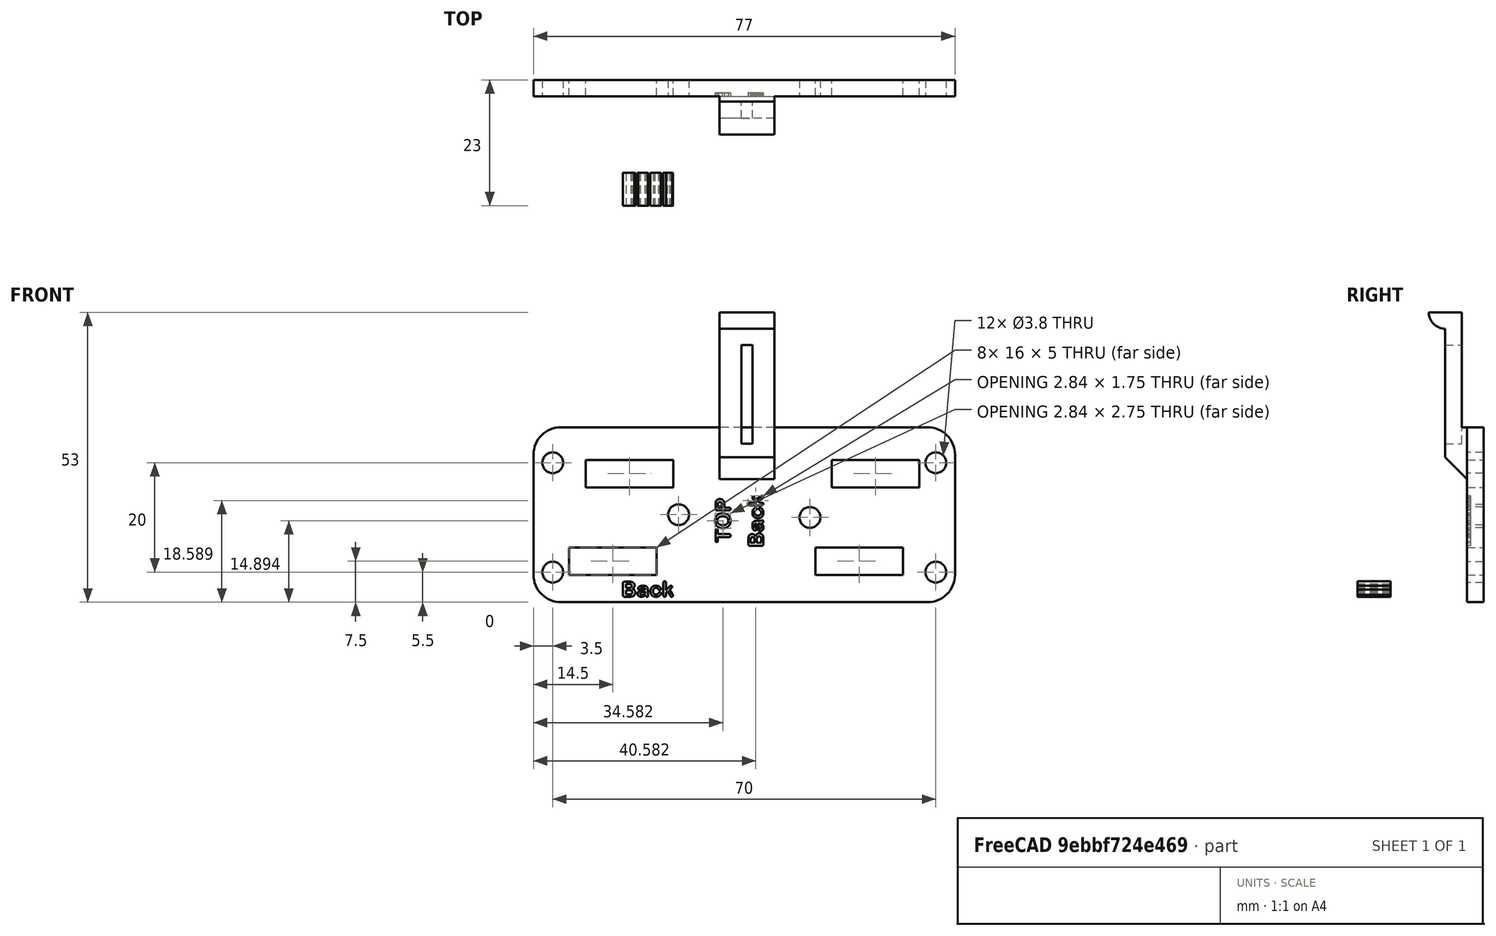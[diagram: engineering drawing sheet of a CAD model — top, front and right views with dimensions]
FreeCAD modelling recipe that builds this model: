
FCSTD DOCUMENT  (FreeCAD 0.16R6712 (Git))
Label: ParkingNozzleBackPlateLeft
License: All rights reserved
LicenseURL: http://en.wikipedia.org/wiki/All_rights_reserved
objects: Part::Cylinder×14, Part::MultiFuse×10, Part::Box×9, Part::Cut×9, Part::Feature×4, Part::Part2DObjectPython×2, Part::Extrusion×1
note: 49 computed .brp shape members not serialized (recipe doc carries the construction recipe); baked Part::Feature solids carry a one-line shape summary decoded from their .brp

FEATURE [Part::Part2DObjectPython] ShapeString002  # Draft 2D object (typed FeaturePython)
  FontFile = <path>
  Size = 3
  String = TOP
  Tracking = 4
FEATURE [Part::Feature] Extrude001002001  label="Extrude001003"
  Placement = pos=(18,0,11) rot=(0,-1,0;1.5708rad)
  shape: bbox 2.835 x 6 x 7.877 mm, 76 faces, 3 solids (baked)
FEATURE [Part::Part2DObjectPython] ShapeString003  # Draft 2D object (typed FeaturePython)
  FontFile = <path>
  Size = 3
  String = Back
  Tracking = 4
FEATURE [Part::Extrusion] Extrude001002002
  Base = -> ShapeString003
  Dir = (0,0,6)
  Placement = pos=(0,0,0) rot=(1,0,0;1.5708rad)
  Solid = false
FEATURE [Part::Feature] Extrude001002002001  label="Extrude001002003"
  Placement = pos=(24,0,10) rot=(0,-1,0;1.5708rad)
  shape: bbox 2.835 x 6 x 9.142 mm, 140 faces, 4 solids (baked)
FEATURE [Part::Box] Box035  label="Würfel034"
  Height = 32
  Length = 77
  Placement = pos=(-16,14,-1) rot=(0,0,1;0rad)
  Width = 3
FEATURE [Part::MultiFuse] Fusion  label="Label"
  Placement = pos=(2,14.6,-1) rot=(0,0,1;0rad)
  Shapes = -> [Extrude001002002001,Extrude001002001]
FEATURE [Part::Cut] Cut
  Base = -> Box035
  Tool = -> Fusion
FEATURE [Part::Box] Box036  label="Würfel035"
  Height = 21
  Length = 10
  Placement = pos=(0,0,-2) rot=(0,0,1;0rad)
  Width = 3
FEATURE [Part::Feature] Cylinder041  label="Zylinder032"
  Placement = pos=(0,0,-2) rot=(1,0,0;1.5708rad)
  shape: bbox 10 x 6 x 3 mm, 4 faces (baked)
FEATURE [Part::MultiFuse] Fusion026007
  Placement = pos=(28,10,50) rot=(0,1,0;3.14159rad)
  Shapes = -> [Box036,Cylinder041]
FEATURE [Part::Cylinder] Cylinder051  label="Zylinder042"
  Angle = 90
  Height = 40
  Placement = pos=(33,25,29) rot=(1,0,0;1.5708rad)
  Radius = 8
FEATURE [Part::Cylinder] Cylinder052  label="Zylinder043"
  Angle = 90
  Height = 40
  Placement = pos=(33,25,29) rot=(1,0,0;1.5708rad)
  Radius = 5
FEATURE [Part::Cut] Cut011004004
  Base = -> Cylinder051
  Placement = pos=(18,0,-7) rot=(0,-1,0;1.5708rad)
  Tool = -> Cylinder052
FEATURE [Part::Cylinder] Cylinder053  label="Zylinder044"
  Angle = 90
  Height = 40
  Placement = pos=(33,25,29) rot=(1,0,0;1.5708rad)
  Radius = 8
FEATURE [Part::Cylinder] Cylinder054  label="Zylinder045"
  Angle = 90
  Height = 40
  Placement = pos=(33,25,29) rot=(1,0,0;1.5708rad)
  Radius = 5
FEATURE [Part::Cut] Cut011004005
  Base = -> Cylinder053
  Placement = pos=(22,0,33) rot=(0,1,0;3.14159rad)
  Tool = -> Cylinder054
FEATURE [Part::Cylinder] Cylinder055  label="Zylinder046"
  Angle = 90
  Height = 40
  Placement = pos=(33,25,29) rot=(1,0,0;1.5708rad)
  Radius = 8
FEATURE [Part::Cylinder] Cylinder056  label="Zylinder047"
  Angle = 90
  Height = 40
  Placement = pos=(33,25,29) rot=(1,0,0;1.5708rad)
  Radius = 5
FEATURE [Part::Cut] Cut011004006
  Base = -> Cylinder055
  Placement = pos=(23,0,-3) rot=(0,0,1;0rad)
  Tool = -> Cylinder056
FEATURE [Part::Cylinder] Cylinder059  label="Zylinder050"
  Angle = 90
  Height = 40
  Placement = pos=(33,25,29) rot=(1,0,0;1.5708rad)
  Radius = 8
FEATURE [Part::Cylinder] Cylinder060  label="Zylinder051"
  Angle = 90
  Height = 40
  Placement = pos=(33,25,29) rot=(1,0,0;1.5708rad)
  Radius = 5
FEATURE [Part::Cut] Cut011004008
  Base = -> Cylinder059
  Placement = pos=(27,0,37) rot=(0,1,0;1.5708rad)
  Tool = -> Cylinder060
FEATURE [Part::MultiFuse] Fusion026012  label="RoundEdges"
  Shapes = -> [Cut011004008,Cut011004006,Cut011004004,Cut011004005]
FEATURE [Part::Box] Box039  label="Würfel038"
  Height = 10
  Length = 10
  Width = 4
FEATURE [Part::Box] Box040  label="Würfel039"
  Height = 10
  Length = 10
  Placement = pos=(0,-5,9) rot=(-1,0,0;0.785398rad)
  Width = 6
FEATURE [Part::Cut] Cut011004010
  Base = -> Box039
  Placement = pos=(28,10,31) rot=(0,1,0;3.14159rad)
  Tool = -> Box040
FEATURE [Part::Box] Box042  label="Würfel041"
  Height = 18
  Length = 2
  Placement = pos=(22,-1,28) rot=(0,0,1;0rad)
  Width = 14
FEATURE [Part::MultiFuse] Fusion026013
  Shapes = -> [Fusion026007,Cut011004010]
FEATURE [Part::Cut] Cut011004011  label="DecuplerLeft"
  Base = -> Fusion026013
  Tool = -> Box042
FEATURE [Part::Cylinder] Cylinder034  label="Zylinder025"
  Angle = 360
  Height = 26
  Placement = pos=(-13,16,4.5) rot=(1,0,0;1.5708rad)
  Radius = 1.9
FEATURE [Part::Cylinder] Cylinder035  label="Zylinder026"
  Angle = 360
  Height = 26
  Placement = pos=(-13,16,24.5) rot=(1,0,0;1.5708rad)
  Radius = 1.9
FEATURE [Part::Cylinder] Cylinder036  label="Zylinder027"
  Angle = 360
  Height = 26
  Placement = pos=(10.5,16,15) rot=(1,0,0;1.5708rad)
  Radius = 1.9
FEATURE [Part::MultiFuse] Fusion026003
  Placement = pos=(0.5,0,0) rot=(0,0,1;0rad)
  Shapes = -> [Cylinder034,Cylinder035]
FEATURE [Part::Cylinder] Cylinder037  label="Zylinder028"
  Angle = 360
  Height = 26
  Placement = pos=(-13,16,4.5) rot=(1,0,0;1.5708rad)
  Radius = 1.9
FEATURE [Part::Cylinder] Cylinder038  label="Zylinder029"
  Angle = 360
  Height = 26
  Placement = pos=(-13,16,24.5) rot=(1,0,0;1.5708rad)
  Radius = 1.9
FEATURE [Part::MultiFuse] Fusion026004
  Placement = pos=(70.5,0,0) rot=(0,0,1;0rad)
  Shapes = -> [Cylinder037,Cylinder038]
FEATURE [Part::Cylinder] Cylinder039  label="Zylinder030"
  Angle = 360
  Height = 26
  Placement = pos=(34.5,16,14.5) rot=(1,0,0;1.5708rad)
  Radius = 1.9
FEATURE [Part::MultiFuse] Fusion026005  label="Bohrung"
  Placement = pos=(0,3,0) rot=(0,0,1;0rad)
  Shapes = -> [Cylinder036,Fusion026003,Fusion026004,Cylinder039]
FEATURE [Part::MultiFuse] Fusion026015
  Shapes = -> [Fusion026012,Fusion026005]
FEATURE [Part::Cut] Cut011004013  label="BasePlate"
  Base = -> Cut
  Tool = -> Fusion026015
FEATURE [Part::MultiFuse] Fusion026016  label="DecuplingPlateLeft"
  Shapes = -> [Cut011004011,Cut011004013]
FEATURE [Part::Box] Box034  label="Würfel033"
  Height = 5
  Length = 16
  Placement = pos=(-9.5,-18,4) rot=(0,0,1;0rad)
  Width = 10
FEATURE [Part::Box] Box043  label="Würfel042"
  Height = 5
  Length = 16
  Placement = pos=(35.5,-18,4) rot=(0,0,1;0rad)
  Width = 10
FEATURE [Part::Box] Box044  label="Würfel043"
  Height = 5
  Length = 16
  Placement = pos=(-6.5,-18,20) rot=(0,0,1;0rad)
  Width = 10
FEATURE [Part::Box] Box037  label="Würfel036"
  Height = 5
  Length = 16
  Placement = pos=(38.5,-18,20) rot=(0,0,1;0rad)
  Width = 10
FEATURE [Part::MultiFuse] Fusion026017  label="SripperHoles"
  Placement = pos=(0,26,0) rot=(0,0,1;0rad)
  Shapes = -> [Box034,Box037,Box043,Box044]
FEATURE [Part::Cut] Cut011004014  label="BackPlateLeft"
  Base = -> Fusion026016
  Tool = -> Fusion026017
FEATURE [Part::Feature] Cut011004014001  label="BackPlateLeft_export"
  shape: bbox 77 x 10 x 53 mm, 258 faces (baked)
note: 2 file-system paths scrubbed to <path> (originals preserved in the JSON sidecar)
